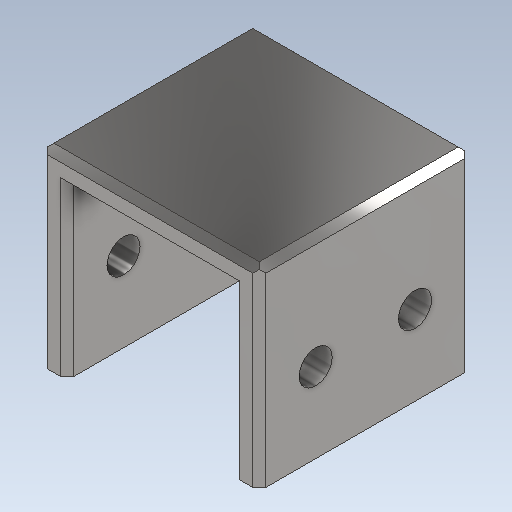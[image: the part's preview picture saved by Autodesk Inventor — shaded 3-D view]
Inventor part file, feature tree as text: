
AUTODESK INVENTOR PART (.ipt)
format: ipt  version: 2021 (Build 250183000, 183)  size: 213,504 bytes
history: native  units: mm
features: sketch x4, extrude x3, chamfer x2, hole x1, fillet x1
ambient origin geometry x8: Origin, YZ Plane, XZ Plane, XY Plane, X Axis, Y Axis, Z Axis, Center Point
bodies: Solid1 (feature_tree)
feature tree (11):
  extrude  "clamp_base"  Depth=66.0mm
  extrude  "clamp_extrusion"  TaperAngle=0.0deg  [1 undecoded]
  extrude  "platform"  Depth=50.0mm
  hole  "clampHole"  [1 undecoded]
  fillet  "Fillet1"  [1 undecoded]
  chamfer  "Chamfer1"  Distance=1149.0mm
  chamfer  "Chamfer2"  Distance=15.0mm
  sketch  "Sketch1"  dims[d0=58.0mm d1=66.0mm]
  sketch  "Sketch2"  dims[d2=33.0mm d3=0.0mm]
  sketch  "Sketch4"  dims[d4=64.0mm d5=0.0mm d6=50.0mm]
  sketch  "Sketch8"  dims[d7=50.0mm d8=25.0mm d9=0.0mm d10=0.0mm d12=1149.0mm d13=15.0mm d14=0.0mm d15=51.0mm d35=0.0mm d36=0.0mm d37=0.0mm d38=0.0mm d51=17.0mm d53=10.0mm d54=6.0mm d55=4.0mm d56=2.0mm d57=90.0deg d58=8.0mm d59=20.594885mm d60=30.0mm d61=64.0mm d81=2.0mm d82=2.0mm d83=2.0mm d84=45.0deg d90=2.0mm d91=2.0mm d92=45.0deg]
note: 3 required parameter values undecoded (feature->parameter linkage not recoverable at this tier; creation-order binding heuristic only, values carry confidence <= 0.55)
